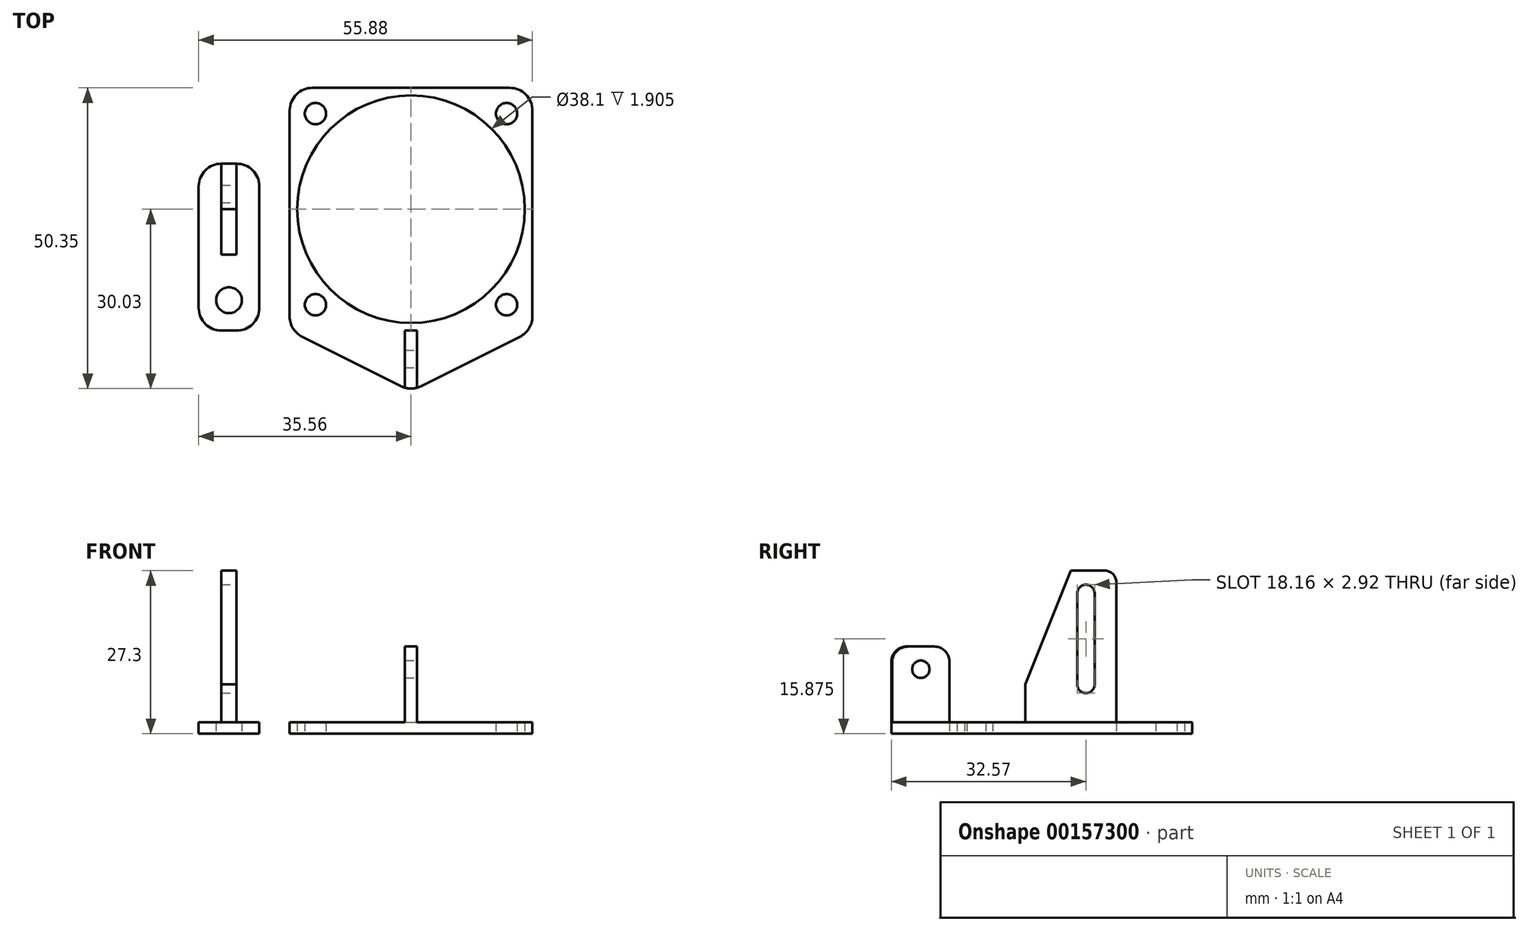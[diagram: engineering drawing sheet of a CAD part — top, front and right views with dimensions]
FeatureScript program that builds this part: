
annotation { "Feature Type Name" : "Feature", "Feature Type Description" : "" }
export const myFeature = defineFeature(function(context is Context, id is Id, definition is map)
    precondition{}
    {
        {
            var Q0;
            Q0=qCreatedBy(makeId("Top.planeOp"),FACE);
            var sketch = newSketch(context, id + "F0", { "sketchPlane" : qUnion([Q0])});
            skLineSegment(sketch, "E0", {"start": v(0, 2.35) * mm, "end": v(0, 36.83) * mm});
            skLineSegment(sketch, "E1", {"start": v(3.8, 40.64) * mm, "end": v(36.83, 40.64) * mm});
            skLineSegment(sketch, "E2", {"start": v(40.64, 36.83) * mm, "end": v(40.64, 2.35) * mm});
            skCircle(sketch, "E3", {"center": v(4.32, 36.32) * mm, "radius": 1.78 * mm});
            skCircle(sketch, "E4", {"center": v(36.32, 36.32) * mm, "radius": 1.78 * mm});
            skCircle(sketch, "E5", {"center": v(4.32, 4.32) * mm, "radius": 1.78 * mm});
            skCircle(sketch, "E6", {"center": v(36.32, 4.32) * mm, "radius": 1.78 * mm});
            skPoint(sketch, "E7.visualSharp", {"position": v(0, 40.64) * mm});
            skArc(sketch, "E7.filletArc", {"start": v(3.81, 40.64) * mm, "mid": v(1.12, 39.52) * mm, "end": v(0, 36.83) * mm});
            skPoint(sketch, "E8.visualSharp", {"position": v(40.64, 40.64) * mm});
            skArc(sketch, "E8.filletArc", {"start": v(40.64, 36.83) * mm, "mid": v(39.52, 39.52) * mm, "end": v(36.83, 40.64) * mm});
            skCircle(sketch, "E9", {"center": v(20.32, 20.32) * mm, "radius": 19.05 * mm});
            skLineSegment(sketch, "E10", {"start": v(2.1, -1.05) * mm, "end": v(18.62, -9.3) * mm});
            skLineSegment(sketch, "E11", {"start": v(22.02, -9.3) * mm, "end": v(38.53, -1.05) * mm});
            skPoint(sketch, "E12.visualSharp", {"position": v(20.32, -10.16) * mm});
            skArc(sketch, "E12.filletArc", {"start": v(18.62, -9.3) * mm, "mid": v(20.32, -9.71) * mm, "end": v(22.02, -9.3) * mm});
            skPoint(sketch, "E13.visualSharp", {"position": v(40.64, 0) * mm});
            skArc(sketch, "E13.filletArc", {"start": v(38.53, -1.05) * mm, "mid": v(40.07, 0.35) * mm, "end": v(40.64, 2.35) * mm});
            skPoint(sketch, "E14.visualSharp", {"position": v(0, 0) * mm});
            skArc(sketch, "E14.filletArc", {"start": v(0, 2.35) * mm, "mid": v(0.57, 0.35) * mm, "end": v(2.1, -1.05) * mm});
            skLineSegment(sketch, "E15.bottom", {"start": v(-8.89, 0) * mm, "end": v(-11.43, 0) * mm});
            skLineSegment(sketch, "E15.top", {"start": v(-8.9, 27.94) * mm, "end": v(-11.43, 27.94) * mm});
            skLineSegment(sketch, "E15.left", {"start": v(-5.08, 3.81) * mm, "end": v(-5.08, 24.13) * mm});
            skLineSegment(sketch, "E15.right", {"start": v(-15.24, 3.81) * mm, "end": v(-15.24, 24.13) * mm});
            skCircle(sketch, "E16", {"center": v(-10.16, 5.08) * mm, "radius": 2.16 * mm});
            skPoint(sketch, "E17.visualSharp", {"position": v(-5.08, 27.94) * mm});
            skArc(sketch, "E17.filletArc", {"start": v(-5.08, 24.13) * mm, "mid": v(-6.2, 26.82) * mm, "end": v(-8.9, 27.94) * mm});
            skPoint(sketch, "E18.visualSharp", {"position": v(-15.24, 27.94) * mm});
            skArc(sketch, "E18.filletArc", {"start": v(-11.43, 27.94) * mm, "mid": v(-14.12, 26.82) * mm, "end": v(-15.24, 24.13) * mm});
            skPoint(sketch, "E19.visualSharp", {"position": v(-15.24, 0) * mm});
            skArc(sketch, "E19.filletArc", {"start": v(-15.24, 3.81) * mm, "mid": v(-14.12, 1.12) * mm, "end": v(-11.43, 0) * mm});
            skPoint(sketch, "E20.visualSharp", {"position": v(-5.08, 0) * mm});
            skArc(sketch, "E20.filletArc", {"start": v(-8.89, 0) * mm, "mid": v(-6.2, 1.12) * mm, "end": v(-5.08, 3.81) * mm});
            skSolve(sketch);
        }
        {
            var Q0;
            Q0 = qSketchRegion(id + "F0", true);
            extrude(context, id + "F1", {"entities" : qUnion([Q0]), "depth" : 1.9 * mm});
        }
        {
            var Q0;
            Q0=makeQuery(id+"F1.opExtrude","CAP_FACE",FACE,{"disambiguationData":[OSD([sQuery(id+"F0.wireOp",EDGE,"E0"),sQuery(id+"F0.wireOp",EDGE,"E1"),sQuery(id+"F0.wireOp",EDGE,"E2"),sQuery(id+"F0.wireOp",EDGE,"E3"),sQuery(id+"F0.wireOp",EDGE,"E4"),sQuery(id+"F0.wireOp",EDGE,"E5"),sQuery(id+"F0.wireOp",EDGE,"E6"),sQuery(id+"F0.wireOp",EDGE,"E7.filletArc"),sQuery(id+"F0.wireOp",EDGE,"E8.filletArc"),sQuery(id+"F0.wireOp",EDGE,"E9"),sQuery(id+"F0.wireOp",EDGE,"E10"),sQuery(id+"F0.wireOp",EDGE,"E11"),sQuery(id+"F0.wireOp",EDGE,"E12.filletArc"),sQuery(id+"F0.wireOp",EDGE,"E13.filletArc"),sQuery(id+"F0.wireOp",EDGE,"E14.filletArc")])],"isStart":false});
            var sketch = newSketch(context, id + "F2", { "sketchPlane" : qUnion([Q0])});
            skLineSegment(sketch, "E21.bottom", {"start": v(19.3, 0) * mm, "end": v(21.34, 0) * mm});
            skLineSegment(sketch, "E21.left", {"start": v(19.3, 0) * mm, "end": v(19.3, -9.57) * mm});
            skLineSegment(sketch, "E21.right", {"start": v(21.34, 0) * mm, "end": v(21.34, -9.57) * mm});
            skArc(sketch, "E22", {"start": v(19.3, -9.57) * mm, "mid": v(20.32, -9.7) * mm, "end": v(21.34, -9.57) * mm});
            skSolve(sketch);
        }
        {
            var Q0;
            Q0 = qSketchRegion(id + "F2", true);
            extrude(context, id + "F3", {"entities" : qUnion([Q0]), "operationType" : NewBodyOperationType.ADD, "depth" : 12.7 * mm});
        }
        {
            var Q0;
            Q0=makeQuery(id+"F3.opExtrude","CAP_EDGE",EDGE,{"disambiguationData":[OSD([sQuery(id+"F2.wireOp",EDGE,"E21.bottom")])],"isStart":false});
            var Q1;
            Q1=makeQuery(id+"F3.opExtrude","CAP_EDGE",EDGE,{"disambiguationData":[OSD([sQuery(id+"F2.wireOp",EDGE,"E22")])],"isStart":false});
            fillet(context, id + "F4", {"entities" : qUnion([Q0, Q1]), "radius" : 2.54 * mm, "allowEdgeOverflow" : false});
        }
        {
            var Q0;
            Q0=makeQuery(id+"F3.opExtrude","SWEPT_FACE",FACE,{"disambiguationData":[OSD([sQuery(id+"F2.wireOp",EDGE,"E21.right")])]});
            var sketch = newSketch(context, id + "F5", { "sketchPlane" : qUnion([Q0])});
            skCircle(sketch, "E23", {"center": v(-4.78, 10.8) * mm, "radius": 1.46 * mm});
            skSolve(sketch);
        }
        {
            var Q0;
            Q0 = qSketchRegion(id + "F5", true);
            extrude(context, id + "F6", {"entities" : qUnion([Q0]), "operationType" : NewBodyOperationType.REMOVE, "endBound" : BoundingType.UP_TO_NEXT, "oppositeDirection" : true, "depth" : 25.4 * mm});
        }
        {
            var Q0;
            Q0=makeQuery(id+"F1.opExtrude","CAP_FACE",FACE,{"disambiguationData":[OSD([sQuery(id+"F0.wireOp",EDGE,"E15.bottom"),sQuery(id+"F0.wireOp",EDGE,"E15.top"),sQuery(id+"F0.wireOp",EDGE,"E15.left"),sQuery(id+"F0.wireOp",EDGE,"E15.right"),sQuery(id+"F0.wireOp",EDGE,"E16"),sQuery(id+"F0.wireOp",EDGE,"E17.filletArc"),sQuery(id+"F0.wireOp",EDGE,"E18.filletArc"),sQuery(id+"F0.wireOp",EDGE,"E19.filletArc"),sQuery(id+"F0.wireOp",EDGE,"E20.filletArc")])],"isStart":false});
            var sketch = newSketch(context, id + "F7", { "sketchPlane" : qUnion([Q0])});
            skLineSegment(sketch, "E24.bottom", {"start": v(-8.9, 27.94) * mm, "end": v(-11.43, 27.94) * mm});
            skLineSegment(sketch, "E24.top", {"start": v(-8.89, 12.7) * mm, "end": v(-11.43, 12.7) * mm});
            skLineSegment(sketch, "E24.left", {"start": v(-8.9, 27.94) * mm, "end": v(-8.89, 12.7) * mm});
            skLineSegment(sketch, "E24.right", {"start": v(-11.43, 27.94) * mm, "end": v(-11.43, 12.7) * mm});
            skSolve(sketch);
        }
        {
            var Q0;
            Q0 = qSketchRegion(id + "F7", true);
            extrude(context, id + "F8", {"entities" : qUnion([Q0]), "operationType" : NewBodyOperationType.ADD, "depth" : 25.4 * mm});
        }
        {
            var Q0;
            Q0=makeQuery(id+"F8.opExtrude","SWEPT_FACE",FACE,{"disambiguationData":[OSD([sQuery(id+"F7.wireOp",EDGE,"E24.left")])]});
            var sketch = newSketch(context, id + "F9", { "sketchPlane" : qUnion([Q0])});
            skLineSegment(sketch, "E25", {"start": v(12.7, 8.25) * mm, "end": v(20.32, 27.3) * mm});
            skLineSegment(sketch, "E26", {"start": v(20.32, 27.3) * mm, "end": v(12.7, 27.3) * mm});
            skLineSegment(sketch, "E27", {"start": v(12.7, 27.3) * mm, "end": v(12.7, 8.26) * mm});
            skSolve(sketch);
        }
        {
            var Q0;
            Q0 = qSketchRegion(id + "F9", true);
            extrude(context, id + "F10", {"entities" : qUnion([Q0]), "operationType" : NewBodyOperationType.REMOVE, "endBound" : BoundingType.UP_TO_NEXT, "oppositeDirection" : true, "depth" : 25.4 * mm});
        }
        {
            var Q0;
            Q0=makeQuery(id+"F10.boolean.opBoolean","COPY",EDGE,{"derivedFrom":makeQuery(id+"F10.opExtrude","SWEPT_EDGE",EDGE,{"disambiguationData":[OSD([sQuery(id+"F7.wireOp",EDGE,"E24.left"),sQuery(id+"F9.wireOp",EDGE,"E25"),sQuery(id+"F9.wireOp",EDGE,"E26")])]})});
            var Q1;
            Q1=makeQuery(id+"F8.opExtrude","CAP_EDGE",EDGE,{"disambiguationData":[OSD([sQuery(id+"F7.wireOp",EDGE,"E24.bottom")])],"isStart":false});
            var Q2;
            Q2=makeQuery(id+"F10.boolean.opBoolean","COPY",EDGE,{"derivedFrom":makeQuery(id+"F10.opExtrude","SWEPT_EDGE",EDGE,{"disambiguationData":[OSD([sQuery(id+"F7.wireOp",EDGE,"E24.top"),sQuery(id+"F7.wireOp",EDGE,"E24.left"),sQuery(id+"F9.wireOp",EDGE,"E25"),sQuery(id+"F9.wireOp",EDGE,"E27")])]})});
            fillet(context, id + "F11", {"entities" : qUnion([Q0, Q1, Q2]), "radius" : 1.9 * mm, "tangentPropagation" : true, "allowEdgeOverflow" : false});
        }
        {
            var Q0;
            Q0=makeQuery(id+"F8.opExtrude","SWEPT_FACE",FACE,{"disambiguationData":[OSD([sQuery(id+"F7.wireOp",EDGE,"E24.left")])]});
            var sketch = newSketch(context, id + "F12", { "sketchPlane" : qUnion([Q0])});
            skArc(sketch, "E28", {"start": v(24.32, 23.5) * mm, "mid": v(22.86, 24.96) * mm, "end": v(21.4, 23.5) * mm});
            skArc(sketch, "E29", {"start": v(21.4, 8.26) * mm, "mid": v(22.86, 6.8) * mm, "end": v(24.32, 8.26) * mm});
            skLineSegment(sketch, "E30", {"start": v(24.32, 8.26) * mm, "end": v(24.32, 23.5) * mm});
            skLineSegment(sketch, "E31", {"start": v(21.4, 23.5) * mm, "end": v(21.4, 8.26) * mm});
            skSolve(sketch);
        }
        {
            var Q0;
            Q0 = qSketchRegion(id + "F12", true);
            extrude(context, id + "F13", {"entities" : qUnion([Q0]), "operationType" : NewBodyOperationType.REMOVE, "endBound" : BoundingType.UP_TO_NEXT, "oppositeDirection" : true, "depth" : 25.4 * mm});
        }
    });
